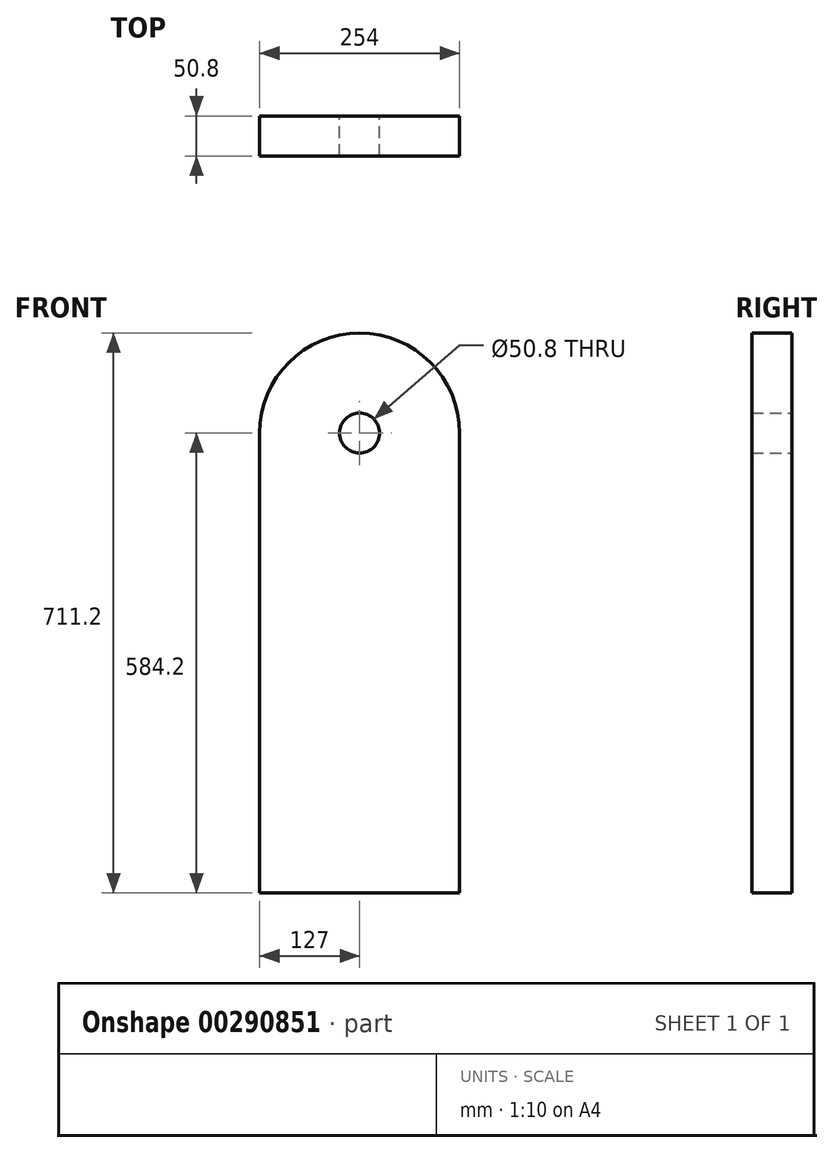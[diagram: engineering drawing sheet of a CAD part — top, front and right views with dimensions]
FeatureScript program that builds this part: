
annotation { "Feature Type Name" : "Feature", "Feature Type Description" : "" }
export const myFeature = defineFeature(function(context is Context, id is Id, definition is map)
    precondition{}
    {
        {
            var Q0;
            Q0=qCreatedBy(makeId("Front.planeOp"),FACE);
            var sketch = newSketch(context, id + "F0", { "sketchPlane" : qUnion([Q0])});
            skLineSegment(sketch, "E0.bottom", {"start": v(0, 0) * mm, "end": v(254, 0) * mm});
            skLineSegment(sketch, "E0.top", {"start": v(127, 711.2) * mm, "end": v(127, 711.2) * mm});
            skLineSegment(sketch, "E0.left", {"start": v(0, 0) * mm, "end": v(0, 584.2) * mm});
            skLineSegment(sketch, "E0.right", {"start": v(254, 0) * mm, "end": v(254, 584.2) * mm});
            skPoint(sketch, "E1.visualSharp", {"position": v(0, 711.2) * mm});
            skArc(sketch, "E1.filletArc", {"start": v(127, 711.2) * mm, "mid": v(37.2, 674) * mm, "end": v(0, 584.2) * mm});
            skPoint(sketch, "E2.visualSharp", {"position": v(254, 711.2) * mm});
            skArc(sketch, "E2.filletArc", {"start": v(254, 584.2) * mm, "mid": v(216.8, 674) * mm, "end": v(127, 711.2) * mm});
            skCircle(sketch, "E3", {"center": v(127, 584.2) * mm, "radius": 25.4 * mm});
            skSolve(sketch);
        }
        {
            var Q0;
            Q0 = qSketchRegion(id + "F0", true);
            extrude(context, id + "F1", {"entities" : qUnion([Q0]), "depth" : 50.8 * mm});
        }
    });
